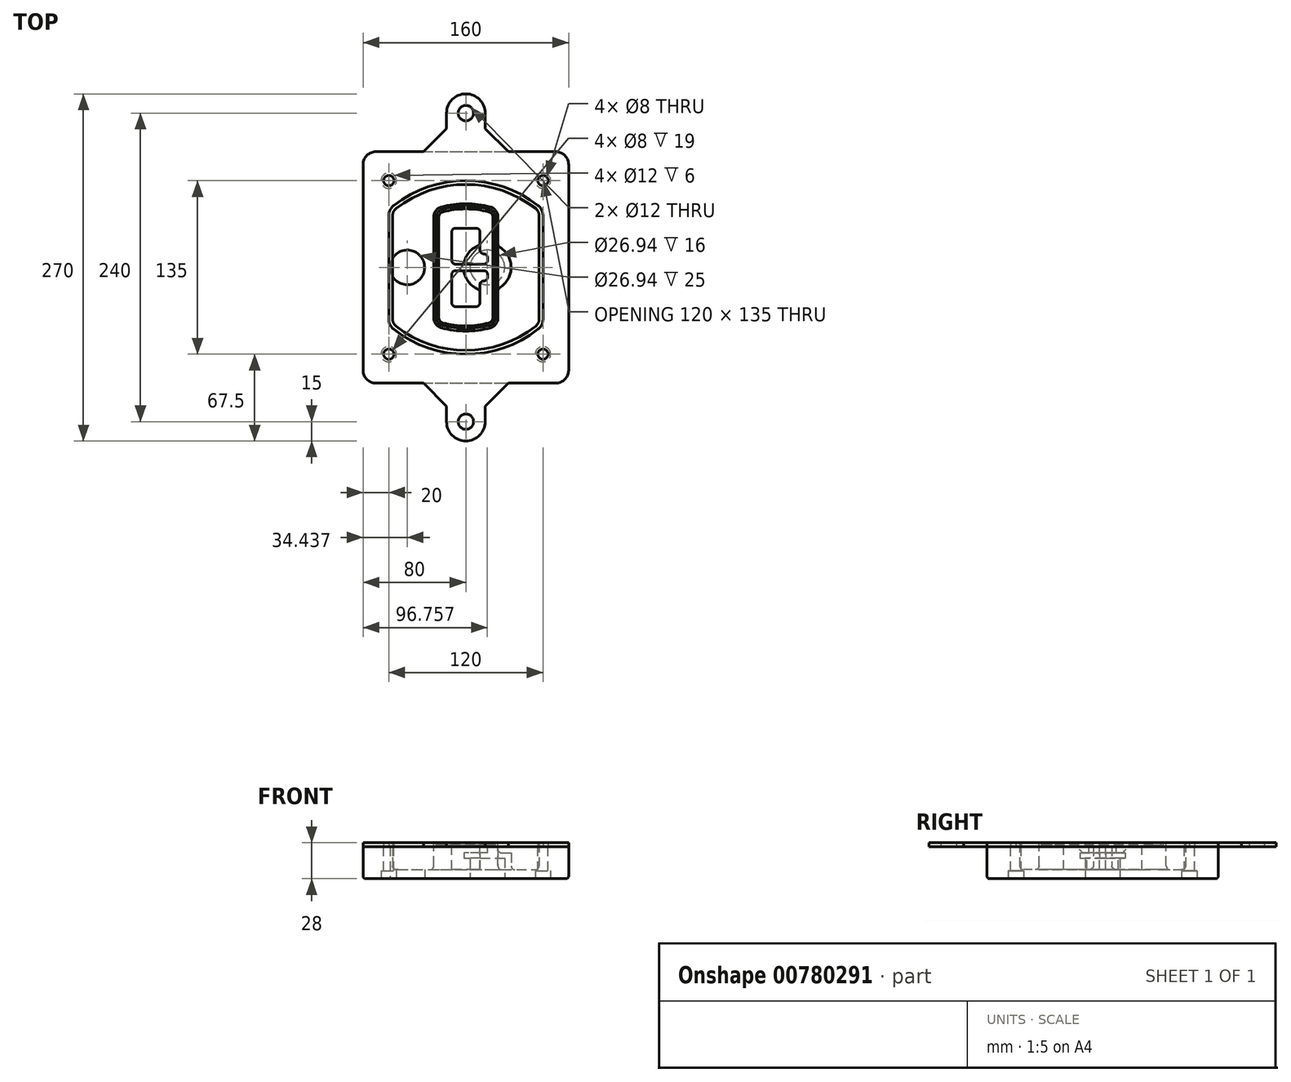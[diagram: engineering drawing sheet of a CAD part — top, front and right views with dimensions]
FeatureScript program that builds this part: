
annotation { "Feature Type Name" : "Feature", "Feature Type Description" : "" }
export const myFeature = defineFeature(function(context is Context, id is Id, definition is map)
    precondition{}
    {
        {
            var Q0;
            Q0=qCreatedBy(makeId("Top.planeOp"),FACE);
            var sketch = newSketch(context, id + "F0", { "sketchPlane" : qUnion([Q0])});
            skPoint(sketch, "E0.rect.middle", {"position": v(0, 0) * mm});
            skLineSegment(sketch, "E1.bottom", {"start": v(-70, -90) * mm, "end": v(70, -90) * mm});
            skLineSegment(sketch, "E1.top", {"start": v(-70, 90) * mm, "end": v(70, 90) * mm});
            skLineSegment(sketch, "E1.left", {"start": v(-80, -80) * mm, "end": v(-80, 80) * mm});
            skLineSegment(sketch, "E1.right", {"start": v(80, -80) * mm, "end": v(80, 80) * mm});
            skLineSegment(sketch, "E2", {"start": v(-80, 90) * mm, "end": v(80, -90) * mm, "construction": true});
            skLineSegment(sketch, "E3", {"start": v(80, 90) * mm, "end": v(-80, -90) * mm, "construction": true});
            skCircle(sketch, "E4", {"center": v(-60, 67.5) * mm, "radius": 4 * mm});
            skCircle(sketch, "E5", {"center": v(60, 67.5) * mm, "radius": 4 * mm});
            skCircle(sketch, "E6", {"center": v(60, -67.5) * mm, "radius": 4 * mm});
            skCircle(sketch, "E7", {"center": v(-60, -67.5) * mm, "radius": 4 * mm});
            skLineSegment(sketch, "E8", {"start": v(-60, 67.5) * mm, "end": v(60, 67.5) * mm, "construction": true});
            skLineSegment(sketch, "E9", {"start": v(60, 67.5) * mm, "end": v(60, -67.5) * mm, "construction": true});
            skLineSegment(sketch, "E10", {"start": v(60, -67.5) * mm, "end": v(-60, -67.5) * mm, "construction": true});
            skLineSegment(sketch, "E11", {"start": v(-60, -67.5) * mm, "end": v(-60, 67.5) * mm, "construction": true});
            skLineSegment(sketch, "E12", {"start": v(-60, 40.3) * mm, "end": v(-60, -40.3) * mm});
            skLineSegment(sketch, "E13", {"start": v(60, 40.3) * mm, "end": v(60, -40.3) * mm});
            skArc(sketch, "E14", {"start": v(56.15, 48.18) * mm, "mid": v(0, 67.5) * mm, "end": v(-56.15, 48.18) * mm});
            skArc(sketch, "E15", {"start": v(-56.15, -48.18) * mm, "mid": v(0, -67.5) * mm, "end": v(56.15, -48.18) * mm});
            skLineSegment(sketch, "E16", {"start": v(-60, 0) * mm, "end": v(60, 0) * mm, "construction": true});
            skPoint(sketch, "E17.visualSharp", {"position": v(-60, -45) * mm});
            skArc(sketch, "E17.filletArc", {"start": v(-60, -40.3) * mm, "mid": v(-58.99, -44.68) * mm, "end": v(-56.15, -48.18) * mm});
            skPoint(sketch, "E18.visualSharp", {"position": v(-60, 45) * mm});
            skArc(sketch, "E18.filletArc", {"start": v(-56.15, 48.18) * mm, "mid": v(-58.99, 44.68) * mm, "end": v(-60, 40.3) * mm});
            skPoint(sketch, "E19.visualSharp", {"position": v(60, 45) * mm});
            skArc(sketch, "E19.filletArc", {"start": v(60, 40.3) * mm, "mid": v(58.99, 44.68) * mm, "end": v(56.15, 48.18) * mm});
            skPoint(sketch, "E20.visualSharp", {"position": v(60, -45) * mm});
            skArc(sketch, "E20.filletArc", {"start": v(56.15, -48.18) * mm, "mid": v(58.99, -44.68) * mm, "end": v(60, -40.3) * mm});
            skPoint(sketch, "E21.visualSharp", {"position": v(-80, 90) * mm});
            skArc(sketch, "E21.filletArc", {"start": v(-70, 90) * mm, "mid": v(-77.07, 87.07) * mm, "end": v(-80, 80) * mm});
            skPoint(sketch, "E22.visualSharp", {"position": v(80, 90) * mm});
            skArc(sketch, "E22.filletArc", {"start": v(80, 80) * mm, "mid": v(77.07, 87.07) * mm, "end": v(70, 90) * mm});
            skPoint(sketch, "E23.visualSharp", {"position": v(80, -90) * mm});
            skArc(sketch, "E23.filletArc", {"start": v(70, -90) * mm, "mid": v(77.07, -87.07) * mm, "end": v(80, -80) * mm});
            skPoint(sketch, "E24.visualSharp", {"position": v(-80, -90) * mm});
            skArc(sketch, "E24.filletArc", {"start": v(-80, -80) * mm, "mid": v(-77.07, -87.07) * mm, "end": v(-70, -90) * mm});
            skArc(sketch, "E25.0", {"start": v(57, 40.3) * mm, "mid": v(56.3, 43.36) * mm, "end": v(54.3, 45.81) * mm});
            skLineSegment(sketch, "E25.1", {"start": v(57, 40.3) * mm, "end": v(57, -40.3) * mm});
            skArc(sketch, "E25.2", {"start": v(54.3, -45.81) * mm, "mid": v(56.3, -43.36) * mm, "end": v(57, -40.3) * mm});
            skArc(sketch, "E25.3", {"start": v(-54.3, -45.81) * mm, "mid": v(0, -64.5) * mm, "end": v(54.3, -45.81) * mm});
            skArc(sketch, "E25.4", {"start": v(-57, -40.3) * mm, "mid": v(-56.3, -43.36) * mm, "end": v(-54.3, -45.81) * mm});
            skArc(sketch, "E25.5", {"start": v(54.3, 45.81) * mm, "mid": v(0, 64.5) * mm, "end": v(-54.3, 45.81) * mm});
            skLineSegment(sketch, "E25.6", {"start": v(-57, 40.3) * mm, "end": v(-57, -40.3) * mm});
            skArc(sketch, "E25.7", {"start": v(-54.3, 45.81) * mm, "mid": v(-56.3, 43.36) * mm, "end": v(-57, 40.3) * mm});
            skArc(sketch, "E26.0", {"start": v(-58.62, 51.33) * mm, "mid": v(-62.58, 46.43) * mm, "end": v(-64, 40.3) * mm});
            skArc(sketch, "E26.1", {"start": v(58.62, 51.33) * mm, "mid": v(0, 71.5) * mm, "end": v(-58.62, 51.33) * mm});
            skArc(sketch, "E26.2", {"start": v(64, 40.3) * mm, "mid": v(62.58, 46.43) * mm, "end": v(58.62, 51.33) * mm});
            skLineSegment(sketch, "E26.3", {"start": v(64, 40.3) * mm, "end": v(64, -40.3) * mm});
            skArc(sketch, "E26.4", {"start": v(58.62, -51.33) * mm, "mid": v(62.58, -46.43) * mm, "end": v(64, -40.3) * mm});
            skLineSegment(sketch, "E26.5", {"start": v(-64, 40.3) * mm, "end": v(-64, -40.3) * mm});
            skArc(sketch, "E26.6", {"start": v(-58.62, -51.33) * mm, "mid": v(0, -71.5) * mm, "end": v(58.62, -51.33) * mm});
            skArc(sketch, "E26.7", {"start": v(-64, -40.3) * mm, "mid": v(-62.58, -46.43) * mm, "end": v(-58.62, -51.33) * mm});
            skSolve(sketch);
        }
        {
            var Q0;
            Q0=makeQuery(id+"F0.imprint","IMPRINT",FACE,{"disambiguationData":[TD([[makeQuery(id+"F0.imprint","IMPRINT",EDGE,{"derivedFrom":sQuery(id+"F0.wireOp",EDGE,"E1.bottom")}),1.0]])]});
            var Q1;
            Q1=makeQuery(id+"F0.imprint","IMPRINT",FACE,{"disambiguationData":[TD([[makeQuery(id+"F0.imprint","IMPRINT",EDGE,{"derivedFrom":sQuery(id+"F0.wireOp",EDGE,"E12")}),1.0]])]});
            var Q2;
            Q2=makeQuery(id+"F0.imprint","IMPRINT",FACE,{"disambiguationData":[TD([[makeQuery(id+"F0.imprint","IMPRINT",EDGE,{"derivedFrom":sQuery(id+"F0.wireOp",EDGE,"E25.0")}),1.0]])]});
            var Q3;
            Q3=makeQuery(id+"F0.imprint","IMPRINT",FACE,{"disambiguationData":[TD([[makeQuery(id+"F0.imprint","IMPRINT",EDGE,{"derivedFrom":sQuery(id+"F0.wireOp",EDGE,"E12")}),-1.0]])]});
            extrude(context, id + "F1", {"entities" : qUnion([Q0, Q1, Q2, Q3]), "oppositeDirection" : true, "depth" : 25 * mm});
        }
        {
            var Q0;
            Q0=makeQuery(id+"F0.imprint","IMPRINT",FACE,{"disambiguationData":[TD([[makeQuery(id+"F0.imprint","IMPRINT",EDGE,{"derivedFrom":sQuery(id+"F0.wireOp",EDGE,"E12")}),1.0]])]});
            extrude(context, id + "F2", {"entities" : qUnion([Q0]), "operationType" : NewBodyOperationType.ADD, "depth" : 3 * mm});
        }
        {
            var Q0;
            Q0=makeQuery(id+"F0.imprint","IMPRINT",FACE,{"disambiguationData":[TD([[makeQuery(id+"F0.imprint","IMPRINT",EDGE,{"derivedFrom":sQuery(id+"F0.wireOp",EDGE,"E25.0")}),1.0]])]});
            extrude(context, id + "F3", {"entities" : qUnion([Q0]), "operationType" : NewBodyOperationType.REMOVE, "oppositeDirection" : true, "depth" : 18 * mm});
        }
        {
            var Q0;
            Q0=makeQuery(id+"F2.opExtrude","CAP_FACE",FACE,{"disambiguationData":[OSD([sQuery(id+"F0.wireOp",EDGE,"E12"),sQuery(id+"F0.wireOp",EDGE,"E13"),sQuery(id+"F0.wireOp",EDGE,"E14"),sQuery(id+"F0.wireOp",EDGE,"E15"),sQuery(id+"F0.wireOp",EDGE,"E17.filletArc"),sQuery(id+"F0.wireOp",EDGE,"E18.filletArc"),sQuery(id+"F0.wireOp",EDGE,"E19.filletArc"),sQuery(id+"F0.wireOp",EDGE,"E20.filletArc"),sQuery(id+"F0.wireOp",EDGE,"E25.0"),sQuery(id+"F0.wireOp",EDGE,"E25.1"),sQuery(id+"F0.wireOp",EDGE,"E25.2"),sQuery(id+"F0.wireOp",EDGE,"E25.3"),sQuery(id+"F0.wireOp",EDGE,"E25.4"),sQuery(id+"F0.wireOp",EDGE,"E25.5"),sQuery(id+"F0.wireOp",EDGE,"E25.6"),sQuery(id+"F0.wireOp",EDGE,"E25.7")])],"isStart":false});
            var sketch = newSketch(context, id + "F4", { "sketchPlane" : qUnion([Q0])});
            skArc(sketch, "E27.0", {"start": v(-19.08, -46.97) * mm, "mid": v(0, -49.5) * mm, "end": v(19.08, -46.97) * mm});
            skArc(sketch, "E28.0", {"start": v(19.08, 46.97) * mm, "mid": v(0, 49.5) * mm, "end": v(-19.08, 46.97) * mm});
            skLineSegment(sketch, "E29", {"start": v(-25, 39.25) * mm, "end": v(-25, -39.25) * mm});
            skLineSegment(sketch, "E30", {"start": v(25, 39.25) * mm, "end": v(25, -39.25) * mm});
            skLineSegment(sketch, "E31", {"start": v(-25, 45.1) * mm, "end": v(25, 45.1) * mm, "construction": true});
            skLineSegment(sketch, "E32", {"start": v(-25, -45.1) * mm, "end": v(25, -45.1) * mm, "construction": true});
            skPoint(sketch, "E33.visualSharp", {"position": v(-25, 45.1) * mm});
            skArc(sketch, "E33.filletArc", {"start": v(-19.08, 46.97) * mm, "mid": v(-23.35, 44.11) * mm, "end": v(-25, 39.25) * mm});
            skPoint(sketch, "E34.visualSharp", {"position": v(25, 45.1) * mm});
            skArc(sketch, "E34.filletArc", {"start": v(25, 39.25) * mm, "mid": v(23.35, 44.11) * mm, "end": v(19.08, 46.97) * mm});
            skPoint(sketch, "E35.visualSharp", {"position": v(25, -45.1) * mm});
            skArc(sketch, "E35.filletArc", {"start": v(19.08, -46.97) * mm, "mid": v(23.35, -44.11) * mm, "end": v(25, -39.25) * mm});
            skPoint(sketch, "E36.visualSharp", {"position": v(-25, -45.1) * mm});
            skArc(sketch, "E36.filletArc", {"start": v(-25, -39.25) * mm, "mid": v(-23.35, -44.11) * mm, "end": v(-19.08, -46.97) * mm});
            skArc(sketch, "E37.0", {"start": v(54.3, 45.81) * mm, "mid": v(0, 64.5) * mm, "end": v(-54.3, 45.81) * mm});
            skArc(sketch, "E37.1", {"start": v(-54.3, 45.81) * mm, "mid": v(-56.3, 43.36) * mm, "end": v(-57, 40.3) * mm});
            skLineSegment(sketch, "E37.2", {"start": v(-57, 40.3) * mm, "end": v(-57, -40.3) * mm});
            skArc(sketch, "E37.3", {"start": v(-57, -40.3) * mm, "mid": v(-56.3, -43.36) * mm, "end": v(-54.3, -45.81) * mm});
            skArc(sketch, "E37.4", {"start": v(-54.3, -45.81) * mm, "mid": v(0, -64.5) * mm, "end": v(54.3, -45.81) * mm});
            skArc(sketch, "E37.5", {"start": v(54.3, -45.81) * mm, "mid": v(56.3, -43.36) * mm, "end": v(57, -40.3) * mm});
            skLineSegment(sketch, "E37.6", {"start": v(57, 40.3) * mm, "end": v(57, -40.3) * mm});
            skArc(sketch, "E37.7", {"start": v(57, 40.3) * mm, "mid": v(56.3, 43.36) * mm, "end": v(54.3, 45.81) * mm});
            skLineSegment(sketch, "E38.0", {"start": v(23, 39.25) * mm, "end": v(23, -39.25) * mm});
            skArc(sketch, "E38.1", {"start": v(18.56, -45.04) * mm, "mid": v(21.76, -42.9) * mm, "end": v(23, -39.25) * mm});
            skArc(sketch, "E38.2", {"start": v(-18.56, -45.04) * mm, "mid": v(0, -47.5) * mm, "end": v(18.56, -45.04) * mm});
            skArc(sketch, "E38.3", {"start": v(-23, -39.25) * mm, "mid": v(-21.76, -42.9) * mm, "end": v(-18.56, -45.04) * mm});
            skLineSegment(sketch, "E38.4", {"start": v(-23, 39.25) * mm, "end": v(-23, -39.25) * mm});
            skArc(sketch, "E38.5", {"start": v(23, 39.25) * mm, "mid": v(21.76, 42.9) * mm, "end": v(18.56, 45.04) * mm});
            skArc(sketch, "E38.6", {"start": v(-18.56, 45.04) * mm, "mid": v(-21.76, 42.9) * mm, "end": v(-23, 39.25) * mm});
            skArc(sketch, "E38.7", {"start": v(18.56, 45.04) * mm, "mid": v(0, 47.5) * mm, "end": v(-18.56, 45.04) * mm});
            skArc(sketch, "E39.0", {"start": v(21, 39.25) * mm, "mid": v(20.18, 41.68) * mm, "end": v(18.04, 43.1) * mm});
            skLineSegment(sketch, "E39.1", {"start": v(21, 39.25) * mm, "end": v(21, -39.25) * mm});
            skArc(sketch, "E39.2", {"start": v(18.04, -43.1) * mm, "mid": v(20.18, -41.68) * mm, "end": v(21, -39.25) * mm});
            skArc(sketch, "E39.3", {"start": v(-18.04, -43.1) * mm, "mid": v(0, -45.5) * mm, "end": v(18.04, -43.1) * mm});
            skArc(sketch, "E39.4", {"start": v(-21, -39.25) * mm, "mid": v(-20.18, -41.68) * mm, "end": v(-18.04, -43.1) * mm});
            skArc(sketch, "E39.5", {"start": v(18.04, 43.1) * mm, "mid": v(0, 45.5) * mm, "end": v(-18.04, 43.1) * mm});
            skLineSegment(sketch, "E39.6", {"start": v(-21, 39.25) * mm, "end": v(-21, -39.25) * mm});
            skArc(sketch, "E39.7", {"start": v(-18.04, 43.1) * mm, "mid": v(-20.18, 41.68) * mm, "end": v(-21, 39.25) * mm});
            skLineSegment(sketch, "E40", {"start": v(-25, 0) * mm, "end": v(25, 0) * mm, "construction": true});
            skLineSegment(sketch, "E41", {"start": v(-11, 5.5) * mm, "end": v(-11, 27.5) * mm});
            skLineSegment(sketch, "E42", {"start": v(-8, 30.5) * mm, "end": v(8, 30.5) * mm});
            skLineSegment(sketch, "E43", {"start": v(11, 27.5) * mm, "end": v(11, 13.5) * mm});
            skLineSegment(sketch, "E44", {"start": v(14, 10.5) * mm, "end": v(14, 10.5) * mm});
            skLineSegment(sketch, "E45", {"start": v(17, 7.5) * mm, "end": v(17, 5.5) * mm});
            skLineSegment(sketch, "E46", {"start": v(14, 2.5) * mm, "end": v(-8, 2.5) * mm});
            skPoint(sketch, "E47.visualSharp", {"position": v(-11, 30.5) * mm});
            skArc(sketch, "E47.filletArc", {"start": v(-8, 30.5) * mm, "mid": v(-10.12, 29.62) * mm, "end": v(-11, 27.5) * mm});
            skPoint(sketch, "E48.visualSharp", {"position": v(11, 30.5) * mm});
            skArc(sketch, "E48.filletArc", {"start": v(11, 27.5) * mm, "mid": v(10.12, 29.62) * mm, "end": v(8, 30.5) * mm});
            skPoint(sketch, "E49.visualSharp", {"position": v(11, 10.5) * mm});
            skArc(sketch, "E49.filletArc", {"start": v(11, 13.5) * mm, "mid": v(11.88, 11.38) * mm, "end": v(14, 10.5) * mm});
            skPoint(sketch, "E50.visualSharp", {"position": v(17, 10.5) * mm});
            skArc(sketch, "E50.filletArc", {"start": v(17, 7.5) * mm, "mid": v(16.12, 9.62) * mm, "end": v(14, 10.5) * mm});
            skPoint(sketch, "E51.visualSharp", {"position": v(17, 2.5) * mm});
            skArc(sketch, "E51.filletArc", {"start": v(14, 2.5) * mm, "mid": v(16.12, 3.38) * mm, "end": v(17, 5.5) * mm});
            skPoint(sketch, "E52.visualSharp", {"position": v(-11, 2.5) * mm});
            skArc(sketch, "E52.filletArc", {"start": v(-11, 5.5) * mm, "mid": v(-10.12, 3.38) * mm, "end": v(-8, 2.5) * mm});
            skLineSegment(sketch, "E53.0.MirrorCS", {"start": v(14, -2.5) * mm, "end": v(-8, -2.5) * mm});
            skArc(sketch, "E54.0.MirrorCS", {"start": v(-11, -5.5) * mm, "mid": v(-10.12, -3.38) * mm, "end": v(-8, -2.5) * mm});
            skLineSegment(sketch, "E55.0.MirrorCS", {"start": v(-11, -5.5) * mm, "end": v(-11, -27.5) * mm});
            skArc(sketch, "E56.0.MirrorCS", {"start": v(-8, -30.5) * mm, "mid": v(-10.12, -29.62) * mm, "end": v(-11, -27.5) * mm});
            skLineSegment(sketch, "E57.0.MirrorCS", {"start": v(-8, -30.5) * mm, "end": v(8, -30.5) * mm});
            skArc(sketch, "E58.0.MirrorCS", {"start": v(11, -27.5) * mm, "mid": v(10.12, -29.62) * mm, "end": v(8, -30.5) * mm});
            skLineSegment(sketch, "E59.0.MirrorCS", {"start": v(11, -27.5) * mm, "end": v(11, -13.5) * mm});
            skArc(sketch, "E60.0.MirrorCS", {"start": v(11, -13.5) * mm, "mid": v(11.88, -11.38) * mm, "end": v(14, -10.5) * mm});
            skArc(sketch, "E61.0.MirrorCS", {"start": v(17, -7.5) * mm, "mid": v(16.12, -9.62) * mm, "end": v(14, -10.5) * mm});
            skLineSegment(sketch, "E62.0.MirrorCS", {"start": v(17, -7.5) * mm, "end": v(17, -5.5) * mm});
            skArc(sketch, "E63.0.MirrorCS", {"start": v(14, -2.5) * mm, "mid": v(16.12, -3.38) * mm, "end": v(17, -5.5) * mm});
            skSolve(sketch);
        }
        {
            var Q0;
            Q0=makeQuery(id+"F4.imprint","IMPRINT",FACE,{"disambiguationData":[TD([[makeQuery(id+"F4.imprint","IMPRINT",EDGE,{"derivedFrom":sQuery(id+"F4.wireOp",EDGE,"E27.0")}),1.0]])]});
            var Q1;
            Q1=makeQuery(id+"F4.imprint","IMPRINT",FACE,{"disambiguationData":[TD([[makeQuery(id+"F4.imprint","IMPRINT",EDGE,{"derivedFrom":sQuery(id+"F4.wireOp",EDGE,"E38.0")}),-1.0]])]});
            var Q2;
            Q2=makeQuery(id+"F4.imprint","IMPRINT",FACE,{"disambiguationData":[TD([[makeQuery(id+"F4.imprint","IMPRINT",EDGE,{"derivedFrom":sQuery(id+"F4.wireOp",EDGE,"E39.0")}),1.0]])]});
            extrude(context, id + "F5", {"entities" : qUnion([Q0, Q1, Q2]), "operationType" : NewBodyOperationType.ADD, "endBound" : BoundingType.UP_TO_NEXT, "oppositeDirection" : true, "depth" : 25 * mm});
        }
        {
            var Q0;
            Q0=makeQuery(id+"F4.imprint","IMPRINT",FACE,{"disambiguationData":[TD([[makeQuery(id+"F4.imprint","IMPRINT",EDGE,{"derivedFrom":sQuery(id+"F4.wireOp",EDGE,"E38.0")}),-1.0]])]});
            extrude(context, id + "F6", {"entities" : qUnion([Q0]), "operationType" : NewBodyOperationType.REMOVE, "oppositeDirection" : true, "depth" : 2 * mm});
        }
        {
            var Q0;
            Q0=makeQuery(id+"F1.opExtrude","CAP_FACE",FACE,{"disambiguationData":[OSD([sQuery(id+"F0.wireOp",EDGE,"E1.bottom"),sQuery(id+"F0.wireOp",EDGE,"E1.top"),sQuery(id+"F0.wireOp",EDGE,"E1.left"),sQuery(id+"F0.wireOp",EDGE,"E1.right"),sQuery(id+"F0.wireOp",EDGE,"E4"),sQuery(id+"F0.wireOp",EDGE,"E5"),sQuery(id+"F0.wireOp",EDGE,"E6"),sQuery(id+"F0.wireOp",EDGE,"E7"),sQuery(id+"F0.wireOp",EDGE,"E21.filletArc"),sQuery(id+"F0.wireOp",EDGE,"E22.filletArc"),sQuery(id+"F0.wireOp",EDGE,"E23.filletArc"),sQuery(id+"F0.wireOp",EDGE,"E24.filletArc")])],"isStart":false});
            var sketch = newSketch(context, id + "F7", { "sketchPlane" : qUnion([Q0])});
            skCircle(sketch, "E64", {"center": v(16.76, 0) * mm, "radius": 13.47 * mm});
            skCircle(sketch, "E65", {"center": v(-45.56, 0) * mm, "radius": 13.47 * mm});
            skLineSegment(sketch, "E66", {"start": v(80, 0) * mm, "end": v(-80, 0) * mm});
            skCircle(sketch, "E67", {"center": v(16.76, 0) * mm, "radius": 18.47 * mm});
            skCircle(sketch, "E68", {"center": v(60, -67.5) * mm, "radius": 6 * mm});
            skCircle(sketch, "E69", {"center": v(-60, -67.5) * mm, "radius": 6 * mm});
            skCircle(sketch, "E70", {"center": v(-60, 67.5) * mm, "radius": 6 * mm});
            skCircle(sketch, "E71", {"center": v(60, 67.5) * mm, "radius": 6 * mm});
            skSolve(sketch);
        }
        {
            var Q0;
            {var subQ1=sQuery(id+"F7.wireOp",EDGE,"E66");var subQ4=sQuery(id+"F7.wireOp",EDGE,"E64");var subQ6=makeQuery(id+"F7.imprint","INTERSECT",VERTEX,{"disambiguationData":[OD(0.0)],"derivedFrom":[subQ4,subQ1]});Q0=makeQuery(id+"F7.imprint","IMPRINT",FACE,{"disambiguationData":[TD([[makeQuery(id+"F7.imprint","IMPRINT",EDGE,{"disambiguationData":[TD([[subQ6,-1.0]])],"derivedFrom":subQ4}),-1.0]])]});}
            var Q1;
            {var subQ0=sQuery(id+"F7.wireOp",EDGE,"E66");var subQ1=sQuery(id+"F7.wireOp",EDGE,"E64");var subQ3=makeQuery(id+"F7.imprint","INTERSECT",VERTEX,{"disambiguationData":[OD(0.0)],"derivedFrom":[subQ1,subQ0]});Q1=makeQuery(id+"F7.imprint","IMPRINT",FACE,{"disambiguationData":[TD([[makeQuery(id+"F7.imprint","IMPRINT",EDGE,{"disambiguationData":[TD([[subQ3,-1.0]])],"derivedFrom":subQ1}),1.0]])]});}
            var Q2;
            {var subQ0=sQuery(id+"F7.wireOp",EDGE,"E66");var subQ1=sQuery(id+"F7.wireOp",EDGE,"E64");var subQ3=makeQuery(id+"F7.imprint","INTERSECT",VERTEX,{"disambiguationData":[OD(0.0)],"derivedFrom":[subQ1,subQ0]});Q2=makeQuery(id+"F7.imprint","IMPRINT",FACE,{"disambiguationData":[TD([[makeQuery(id+"F7.imprint","IMPRINT",EDGE,{"disambiguationData":[TD([[subQ3,1.0]])],"derivedFrom":subQ1}),1.0]])]});}
            var Q3;
            {var subQ1=sQuery(id+"F7.wireOp",EDGE,"E66");var subQ4=sQuery(id+"F7.wireOp",EDGE,"E64");var subQ6=makeQuery(id+"F7.imprint","INTERSECT",VERTEX,{"disambiguationData":[OD(0.0)],"derivedFrom":[subQ4,subQ1]});Q3=makeQuery(id+"F7.imprint","IMPRINT",FACE,{"disambiguationData":[TD([[makeQuery(id+"F7.imprint","IMPRINT",EDGE,{"disambiguationData":[TD([[subQ6,1.0]])],"derivedFrom":subQ4}),-1.0]])]});}
            extrude(context, id + "F8", {"entities" : qUnion([Q0, Q1, Q2, Q3]), "operationType" : NewBodyOperationType.ADD, "oppositeDirection" : true, "depth" : 20 * mm});
        }
        {
            var Q0;
            {var subQ0=sQuery(id+"F7.wireOp",EDGE,"E66");var subQ1=sQuery(id+"F7.wireOp",EDGE,"E64");var subQ3=makeQuery(id+"F7.imprint","INTERSECT",VERTEX,{"disambiguationData":[OD(0.0)],"derivedFrom":[subQ1,subQ0]});Q0=makeQuery(id+"F7.imprint","IMPRINT",FACE,{"disambiguationData":[TD([[makeQuery(id+"F7.imprint","IMPRINT",EDGE,{"disambiguationData":[TD([[subQ3,-1.0]])],"derivedFrom":subQ1}),1.0]])]});}
            var Q1;
            {var subQ0=sQuery(id+"F7.wireOp",EDGE,"E66");var subQ1=sQuery(id+"F7.wireOp",EDGE,"E64");var subQ3=makeQuery(id+"F7.imprint","INTERSECT",VERTEX,{"disambiguationData":[OD(0.0)],"derivedFrom":[subQ1,subQ0]});Q1=makeQuery(id+"F7.imprint","IMPRINT",FACE,{"disambiguationData":[TD([[makeQuery(id+"F7.imprint","IMPRINT",EDGE,{"disambiguationData":[TD([[subQ3,1.0]])],"derivedFrom":subQ1}),1.0]])]});}
            extrude(context, id + "F9", {"entities" : qUnion([Q0, Q1]), "operationType" : NewBodyOperationType.REMOVE, "oppositeDirection" : true, "depth" : 16 * mm});
        }
        {
            var Q0;
            {var subQ0=sQuery(id+"F7.wireOp",EDGE,"E66");var subQ1=sQuery(id+"F7.wireOp",EDGE,"E65");var subQ3=makeQuery(id+"F7.imprint","INTERSECT",VERTEX,{"disambiguationData":[OD(0.0)],"derivedFrom":[subQ1,subQ0]});Q0=makeQuery(id+"F7.imprint","IMPRINT",FACE,{"disambiguationData":[TD([[makeQuery(id+"F7.imprint","IMPRINT",EDGE,{"disambiguationData":[TD([[subQ3,-1.0]])],"derivedFrom":subQ1}),1.0]])]});}
            var Q1;
            {var subQ0=sQuery(id+"F7.wireOp",EDGE,"E66");var subQ1=sQuery(id+"F7.wireOp",EDGE,"E65");var subQ3=makeQuery(id+"F7.imprint","INTERSECT",VERTEX,{"disambiguationData":[OD(0.0)],"derivedFrom":[subQ1,subQ0]});Q1=makeQuery(id+"F7.imprint","IMPRINT",FACE,{"disambiguationData":[TD([[makeQuery(id+"F7.imprint","IMPRINT",EDGE,{"disambiguationData":[TD([[subQ3,1.0]])],"derivedFrom":subQ1}),1.0]])]});}
            extrude(context, id + "F10", {"entities" : qUnion([Q0, Q1]), "operationType" : NewBodyOperationType.REMOVE, "oppositeDirection" : true, "depth" : 25 * mm});
        }
        {
            var Q0;
            Q0=makeQuery(id+"F7.imprint","IMPRINT",FACE,{"disambiguationData":[TD([[makeQuery(id+"F7.imprint","IMPRINT",EDGE,{"derivedFrom":sQuery(id+"F7.wireOp",EDGE,"E68")}),1.0]])]});
            var Q1;
            Q1=makeQuery(id+"F7.imprint","IMPRINT",FACE,{"disambiguationData":[TD([[makeQuery(id+"F7.imprint","IMPRINT",EDGE,{"derivedFrom":makeQuery(id+"F1.opExtrude","CAP_EDGE",EDGE,{"disambiguationData":[OSD([sQuery(id+"F0.wireOp",EDGE,"E5")])],"isStart":false})}),-1.0]])]});
            var Q2;
            Q2=makeQuery(id+"F7.imprint","IMPRINT",FACE,{"disambiguationData":[TD([[makeQuery(id+"F7.imprint","IMPRINT",EDGE,{"derivedFrom":sQuery(id+"F7.wireOp",EDGE,"E69")}),1.0]])]});
            var Q3;
            Q3=makeQuery(id+"F7.imprint","IMPRINT",FACE,{"disambiguationData":[TD([[makeQuery(id+"F7.imprint","IMPRINT",EDGE,{"derivedFrom":makeQuery(id+"F1.opExtrude","CAP_EDGE",EDGE,{"disambiguationData":[OSD([sQuery(id+"F0.wireOp",EDGE,"E4")])],"isStart":false})}),-1.0]])]});
            var Q4;
            Q4=makeQuery(id+"F7.imprint","IMPRINT",FACE,{"disambiguationData":[TD([[makeQuery(id+"F7.imprint","IMPRINT",EDGE,{"derivedFrom":sQuery(id+"F7.wireOp",EDGE,"E70")}),1.0]])]});
            var Q5;
            Q5=makeQuery(id+"F7.imprint","IMPRINT",FACE,{"disambiguationData":[TD([[makeQuery(id+"F7.imprint","IMPRINT",EDGE,{"derivedFrom":makeQuery(id+"F1.opExtrude","CAP_EDGE",EDGE,{"disambiguationData":[OSD([sQuery(id+"F0.wireOp",EDGE,"E7")])],"isStart":false})}),-1.0]])]});
            var Q6;
            Q6=makeQuery(id+"F7.imprint","IMPRINT",FACE,{"disambiguationData":[TD([[makeQuery(id+"F7.imprint","IMPRINT",EDGE,{"derivedFrom":sQuery(id+"F7.wireOp",EDGE,"E71")}),1.0]])]});
            var Q7;
            Q7=makeQuery(id+"F7.imprint","IMPRINT",FACE,{"disambiguationData":[TD([[makeQuery(id+"F7.imprint","IMPRINT",EDGE,{"derivedFrom":makeQuery(id+"F1.opExtrude","CAP_EDGE",EDGE,{"disambiguationData":[OSD([sQuery(id+"F0.wireOp",EDGE,"E6")])],"isStart":false})}),-1.0]])]});
            extrude(context, id + "F11", {"entities" : qUnion([Q0, Q1, Q2, Q3, Q4, Q5, Q6, Q7]), "operationType" : NewBodyOperationType.REMOVE, "oppositeDirection" : true, "depth" : 6 * mm});
        }
        {
            var Q0;
            Q0=makeQuery(id+"F9.boolean.opBoolean","COPY",FACE,{"derivedFrom":makeQuery(id+"F9.opExtrude","CAP_FACE",FACE,{"disambiguationData":[OSD([sQuery(id+"F7.wireOp",EDGE,"E64")])],"isStart":false})});
            var sketch = newSketch(context, id + "F12", { "sketchPlane" : qUnion([Q0])});
            skArc(sketch, "E72.0", {"start": v(11, 17.55) * mm, "mid": v(2.57, 11.82) * mm, "end": v(-1.54, 2.5) * mm});
            skArc(sketch, "E72.1", {"start": v(-1.54, -2.5) * mm, "mid": v(2.57, -11.82) * mm, "end": v(11, -17.55) * mm});
            skLineSegment(sketch, "E73", {"start": v(-1.54, -2.5) * mm, "end": v(14, -2.5) * mm});
            skLineSegment(sketch, "E74.0", {"start": v(14, 2.5) * mm, "end": v(-1.54, 2.5) * mm});
            skArc(sketch, "E74.1", {"start": v(14, 2.5) * mm, "mid": v(16.12, 3.38) * mm, "end": v(17, 5.5) * mm});
            skLineSegment(sketch, "E74.2", {"start": v(17, 7.5) * mm, "end": v(17, 5.5) * mm});
            skArc(sketch, "E74.3", {"start": v(17, 7.5) * mm, "mid": v(16.12, 9.62) * mm, "end": v(14, 10.5) * mm});
            skArc(sketch, "E74.4", {"start": v(11, 13.5) * mm, "mid": v(11.88, 11.38) * mm, "end": v(14, 10.5) * mm});
            skLineSegment(sketch, "E74.5", {"start": v(11, 17.55) * mm, "end": v(11, 13.5) * mm});
            skLineSegment(sketch, "E74.7", {"start": v(14, -2.5) * mm, "end": v(-1.54, -2.5) * mm});
            skArc(sketch, "E74.8", {"start": v(14, -2.5) * mm, "mid": v(16.12, -3.38) * mm, "end": v(17, -5.5) * mm});
            skLineSegment(sketch, "E74.9", {"start": v(17, -7.5) * mm, "end": v(17, -5.5) * mm});
            skArc(sketch, "E74.10", {"start": v(17, -7.5) * mm, "mid": v(16.12, -9.62) * mm, "end": v(14, -10.5) * mm});
            skArc(sketch, "E74.11", {"start": v(11, -13.5) * mm, "mid": v(11.88, -11.38) * mm, "end": v(14, -10.5) * mm});
            skLineSegment(sketch, "E74.12", {"start": v(11, -17.55) * mm, "end": v(11, -13.5) * mm});
            skPoint(sketch, "E75.orphan", {"position": v(11, -27.5) * mm});
            skPoint(sketch, "E76.orphan", {"position": v(-8, -2.5) * mm});
            skPoint(sketch, "E77.orphan", {"position": v(-8, 2.5) * mm});
            skPoint(sketch, "E78.orphan", {"position": v(11, 27.5) * mm});
            skSolve(sketch);
        }
        {
            var Q0;
            {var subQ7=sQuery(id+"F12.wireOp",EDGE,"E72.0");var subQ14=sQuery(id+"F12.wireOp",EDGE,"E72.1");var subQ16=sQuery(id+"F12.wireOp",EDGE,"E74.1");var subQ18=sQuery(id+"F12.wireOp",EDGE,"E74.8");Q0=qUnion([makeQuery(id+"F12.imprint","IMPRINT",FACE,{"disambiguationData":[TD([[makeQuery(id+"F12.imprint","IMPRINT",EDGE,{"derivedFrom":subQ7}),1.0]])]}),makeQuery(id+"F12.imprint","IMPRINT",FACE,{"disambiguationData":[TD([[makeQuery(id+"F12.imprint","IMPRINT",EDGE,{"derivedFrom":subQ14}),1.0]])]}),makeQuery(id+"F12.imprint","IMPRINT",FACE,{"disambiguationData":[TD([[makeQuery(id+"F12.imprint","IMPRINT",EDGE,{"derivedFrom":subQ16}),1.0]])]}),makeQuery(id+"F12.imprint","IMPRINT",FACE,{"disambiguationData":[TD([[makeQuery(id+"F12.imprint","IMPRINT",EDGE,{"derivedFrom":subQ18}),-1.0]])]})]);}
            var Q1;
            Q1=makeQuery(id+"F5.boolean.opBoolean","SPLIT",FACE,{"disambiguationData":[TD([makeQuery(id+"F5.opExtrude","SWEPT_FACE",FACE,{"disambiguationData":[OSD([sQuery(id+"F4.wireOp",EDGE,"E41")])]})])],"derivedFrom":makeQuery(id+"F3.boolean.opBoolean","COPY",FACE,{"derivedFrom":makeQuery(id+"F3.opExtrude","CAP_FACE",FACE,{"disambiguationData":[OSD([sQuery(id+"F0.wireOp",EDGE,"E25.0"),sQuery(id+"F0.wireOp",EDGE,"E25.1"),sQuery(id+"F0.wireOp",EDGE,"E25.2"),sQuery(id+"F0.wireOp",EDGE,"E25.3"),sQuery(id+"F0.wireOp",EDGE,"E25.4"),sQuery(id+"F0.wireOp",EDGE,"E25.5"),sQuery(id+"F0.wireOp",EDGE,"E25.6"),sQuery(id+"F0.wireOp",EDGE,"E25.7")])],"isStart":false})})});
            extrude(context, id + "F13", {"entities" : qUnion([Q0]), "operationType" : NewBodyOperationType.REMOVE, "endBound" : BoundingType.UP_TO_SURFACE, "endBoundEntityFace" : qUnion([Q1]), "depth" : 25 * mm});
        }
        {
            var Q0;
            Q0=makeQuery(id+"F3.boolean.opBoolean","COPY",EDGE,{"derivedFrom":makeQuery(id+"F3.opExtrude","CAP_EDGE",EDGE,{"disambiguationData":[OSD([sQuery(id+"F0.wireOp",EDGE,"E25.6")])],"isStart":false})});
            var Q1;
            Q1=makeQuery(id+"F8.boolean.opBoolean","INTERSECT",EDGE,{"derivedFrom":[makeQuery(id+"F5.opExtrude","SWEPT_FACE",FACE,{"disambiguationData":[OSD([sQuery(id+"F4.wireOp",EDGE,"E30")])]}),makeQuery(id+"F8.opExtrude","CAP_FACE",FACE,{"disambiguationData":[OSD([sQuery(id+"F7.wireOp",EDGE,"E67")])],"isStart":false})]});
            var Q2;
            Q2=makeQuery(id+"F8.boolean.opBoolean","INTERSECT",EDGE,{"disambiguationData":[OD(1.0)],"derivedFrom":[makeQuery(id+"F5.opExtrude","SWEPT_FACE",FACE,{"disambiguationData":[OSD([sQuery(id+"F4.wireOp",EDGE,"E30")])]}),makeQuery(id+"F8.opExtrude","SWEPT_FACE",FACE,{"disambiguationData":[OSD([sQuery(id+"F7.wireOp",EDGE,"E67")])]})]});
            var Q3;
            {var subQ0=sQuery(id+"F4.wireOp",EDGE,"E30");Q3=makeQuery(id+"F8.boolean.opBoolean","SPLIT",EDGE,{"disambiguationData":[TD([makeQuery(id+"F5.opExtrude","SWEPT_FACE",FACE,{"disambiguationData":[OSD([sQuery(id+"F4.wireOp",EDGE,"E35.filletArc")])]})])],"derivedFrom":makeQuery(id+"F5.opExtrude","CAP_EDGE",EDGE,{"disambiguationData":[OSD([subQ0])],"isStart":false})});}
            var Q4;
            {var subQ0=sQuery(id+"F0.wireOp",EDGE,"E25.7");var subQ1=sQuery(id+"F0.wireOp",EDGE,"E25.1");var subQ2=sQuery(id+"F0.wireOp",EDGE,"E25.6");var subQ3=sQuery(id+"F0.wireOp",EDGE,"E25.5");var subQ4=sQuery(id+"F0.wireOp",EDGE,"E25.4");var subQ5=sQuery(id+"F0.wireOp",EDGE,"E25.0");var subQ6=sQuery(id+"F0.wireOp",EDGE,"E25.2");var subQ7=sQuery(id+"F0.wireOp",EDGE,"E25.3");Q4=makeQuery(id+"F8.boolean.opBoolean","INTERSECT",EDGE,{"derivedFrom":[makeQuery(id+"F5.boolean.opBoolean","SPLIT",FACE,{"disambiguationData":[TD([makeQuery(id+"F2.opExtrude","SWEPT_FACE",FACE,{"disambiguationData":[OSD([subQ5])]})])],"derivedFrom":makeQuery(id+"F3.boolean.opBoolean","COPY",FACE,{"derivedFrom":makeQuery(id+"F3.opExtrude","CAP_FACE",FACE,{"disambiguationData":[OSD([subQ5,subQ1,subQ6,subQ7,subQ4,subQ3,subQ2,subQ0])],"isStart":false})})}),makeQuery(id+"F8.opExtrude","SWEPT_FACE",FACE,{"disambiguationData":[OSD([sQuery(id+"F7.wireOp",EDGE,"E67")])]})]});}
            var Q5;
            Q5=makeQuery(id+"F8.boolean.opBoolean","INTERSECT",EDGE,{"disambiguationData":[OD(0.0)],"derivedFrom":[makeQuery(id+"F5.opExtrude","SWEPT_FACE",FACE,{"disambiguationData":[OSD([sQuery(id+"F4.wireOp",EDGE,"E30")])]}),makeQuery(id+"F8.opExtrude","SWEPT_FACE",FACE,{"disambiguationData":[OSD([sQuery(id+"F7.wireOp",EDGE,"E67")])]})]});
            fillet(context, id + "F14", {"entities" : qUnion([Q0, Q1, Q2, Q3, Q4, Q5]), "radius" : 3 * mm, "tangentPropagation" : true, "allowEdgeOverflow" : false});
        }
        {
            var Q0;
            Q0=makeQuery(id+"F1.opExtrude","CAP_EDGE",EDGE,{"disambiguationData":[OSD([sQuery(id+"F0.wireOp",EDGE,"E1.bottom")])],"isStart":false});
            fillet(context, id + "F15", {"entities" : qUnion([Q0]), "radius" : 2 * mm, "tangentPropagation" : true, "allowEdgeOverflow" : false});
        }
        {
            var Q0;
            {var subQ0=sQuery(id+"F0.wireOp",EDGE,"E21.filletArc");var subQ1=sQuery(id+"F0.wireOp",EDGE,"E7");var subQ2=sQuery(id+"F0.wireOp",EDGE,"E6");var subQ3=sQuery(id+"F0.wireOp",EDGE,"E5");var subQ4=sQuery(id+"F0.wireOp",EDGE,"E4");var subQ5=sQuery(id+"F0.wireOp",EDGE,"E22.filletArc");var subQ6=sQuery(id+"F0.wireOp",EDGE,"E1.bottom");var subQ7=sQuery(id+"F0.wireOp",EDGE,"E1.right");var subQ8=sQuery(id+"F0.wireOp",EDGE,"E1.top");var subQ9=sQuery(id+"F0.wireOp",EDGE,"E1.left");var subQ10=sQuery(id+"F0.wireOp",EDGE,"E23.filletArc");var subQ11=sQuery(id+"F0.wireOp",EDGE,"E24.filletArc");Q0=makeQuery(id+"F2.boolean.opBoolean","SPLIT",FACE,{"disambiguationData":[TD([makeQuery(id+"F1.opExtrude","SWEPT_FACE",FACE,{"disambiguationData":[OSD([subQ6])]})])],"derivedFrom":makeQuery(id+"F1.opExtrude","CAP_FACE",FACE,{"disambiguationData":[OSD([subQ6,subQ8,subQ9,subQ7,subQ4,subQ3,subQ2,subQ1,subQ0,subQ5,subQ10,subQ11])],"isStart":true})});}
            var sketch = newSketch(context, id + "F16", { "sketchPlane" : qUnion([Q0])});
            skLineSegment(sketch, "E79.0", {"start": v(-80, -80) * mm, "end": v(-80, 80) * mm});
            skArc(sketch, "E79.1", {"start": v(-80, -80) * mm, "mid": v(-77.07, -87.07) * mm, "end": v(-70, -90) * mm});
            skLineSegment(sketch, "E79.2", {"start": v(-70, -90) * mm, "end": v(-33, -90) * mm});
            skArc(sketch, "E79.3", {"start": v(70, -90) * mm, "mid": v(77.07, -87.07) * mm, "end": v(80, -80) * mm});
            skLineSegment(sketch, "E79.4", {"start": v(80, -80) * mm, "end": v(80, 80) * mm});
            skArc(sketch, "E79.5", {"start": v(80, 80) * mm, "mid": v(77.07, 87.07) * mm, "end": v(70, 90) * mm});
            skLineSegment(sketch, "E79.6", {"start": v(-70, 90) * mm, "end": v(-33, 90) * mm});
            skArc(sketch, "E79.7", {"start": v(-70, 90) * mm, "mid": v(-77.07, 87.07) * mm, "end": v(-80, 80) * mm});
            skLineSegment(sketch, "E79.8", {"start": v(60, 40.3) * mm, "end": v(60, -40.3) * mm});
            skArc(sketch, "E79.9", {"start": v(60, 40.3) * mm, "mid": v(58.99, 44.68) * mm, "end": v(56.15, 48.18) * mm});
            skArc(sketch, "E79.10", {"start": v(56.15, -48.18) * mm, "mid": v(58.99, -44.68) * mm, "end": v(60, -40.3) * mm});
            skArc(sketch, "E79.11", {"start": v(-56.15, -48.18) * mm, "mid": v(0, -67.5) * mm, "end": v(56.15, -48.18) * mm});
            skArc(sketch, "E79.12", {"start": v(-60, -40.3) * mm, "mid": v(-58.99, -44.68) * mm, "end": v(-56.15, -48.18) * mm});
            skLineSegment(sketch, "E79.13", {"start": v(-60, 40.3) * mm, "end": v(-60, -40.3) * mm});
            skArc(sketch, "E79.14", {"start": v(56.15, 48.18) * mm, "mid": v(0, 67.5) * mm, "end": v(-56.15, 48.18) * mm});
            skArc(sketch, "E79.15", {"start": v(-56.15, 48.18) * mm, "mid": v(-58.99, 44.68) * mm, "end": v(-60, 40.3) * mm});
            skCircle(sketch, "E79.16", {"center": v(-60, -67.5) * mm, "radius": 4 * mm});
            skCircle(sketch, "E79.17", {"center": v(-60, 67.5) * mm, "radius": 4 * mm});
            skCircle(sketch, "E79.18", {"center": v(60, 67.5) * mm, "radius": 4 * mm});
            skCircle(sketch, "E79.19", {"center": v(60, -67.5) * mm, "radius": 4 * mm});
            skLineSegment(sketch, "E80", {"start": v(-15, 108) * mm, "end": v(-15, 120) * mm});
            skLineSegment(sketch, "E81", {"start": v(15, 120) * mm, "end": v(15, 108) * mm});
            skLineSegment(sketch, "E82", {"start": v(15, 108) * mm, "end": v(33, 90) * mm});
            skCircle(sketch, "E83", {"center": v(0, 120) * mm, "radius": 6 * mm});
            skLineSegment(sketch, "E84", {"start": v(0, 90) * mm, "end": v(0, 120) * mm, "construction": true});
            skArc(sketch, "E85", {"start": v(15, 120) * mm, "mid": v(0, 135) * mm, "end": v(-15, 120) * mm});
            skLineSegment(sketch, "E86", {"start": v(-15, 108) * mm, "end": v(-33, 90) * mm});
            skLineSegment(sketch, "E87", {"start": v(-80, 0) * mm, "end": v(80, 0) * mm, "construction": true});
            skLineSegment(sketch, "E88.MirrorCS", {"start": v(-15, -108) * mm, "end": v(-15, -120) * mm});
            skLineSegment(sketch, "E89.MirrorCS", {"start": v(-15, -108) * mm, "end": v(-33, -90) * mm});
            skArc(sketch, "E90.MirrorCS", {"start": v(15, -120) * mm, "mid": v(0, -135) * mm, "end": v(-15, -120) * mm});
            skLineSegment(sketch, "E91.MirrorCS", {"start": v(15, -108) * mm, "end": v(33, -90) * mm});
            skLineSegment(sketch, "E92.MirrorCS", {"start": v(0, -90) * mm, "end": v(0, -120) * mm, "construction": true});
            skLineSegment(sketch, "E93.MirrorCS", {"start": v(15, -120) * mm, "end": v(15, -108) * mm});
            skCircle(sketch, "E94.MirrorC", {"center": v(0, -120) * mm, "radius": 6 * mm});
            skLineSegment(sketch, "E95.trimOffspring", {"start": v(33, 90) * mm, "end": v(70, 90) * mm});
            skLineSegment(sketch, "E96.trimOffspring", {"start": v(33, -90) * mm, "end": v(70, -90) * mm});
            skSolve(sketch);
        }
        {
            var Q0;
            Q0 = qSketchRegion(id + "F16", true);
            var Q1;
            Q1=makeQuery(id+"F2.opExtrude","CAP_FACE",FACE,{"disambiguationData":[OSD([sQuery(id+"F0.wireOp",EDGE,"E12"),sQuery(id+"F0.wireOp",EDGE,"E13"),sQuery(id+"F0.wireOp",EDGE,"E14"),sQuery(id+"F0.wireOp",EDGE,"E15"),sQuery(id+"F0.wireOp",EDGE,"E17.filletArc"),sQuery(id+"F0.wireOp",EDGE,"E18.filletArc"),sQuery(id+"F0.wireOp",EDGE,"E19.filletArc"),sQuery(id+"F0.wireOp",EDGE,"E20.filletArc"),sQuery(id+"F0.wireOp",EDGE,"E25.0"),sQuery(id+"F0.wireOp",EDGE,"E25.1"),sQuery(id+"F0.wireOp",EDGE,"E25.2"),sQuery(id+"F0.wireOp",EDGE,"E25.3"),sQuery(id+"F0.wireOp",EDGE,"E25.4"),sQuery(id+"F0.wireOp",EDGE,"E25.5"),sQuery(id+"F0.wireOp",EDGE,"E25.6"),sQuery(id+"F0.wireOp",EDGE,"E25.7")])],"isStart":false});
            extrude(context, id + "F17", {"entities" : qUnion([Q0]), "endBound" : BoundingType.UP_TO_SURFACE, "depth" : 25 * mm, "endBoundEntityFace" : qUnion([Q1]), "offsetDistance" : 25 * mm});
        }
    });
